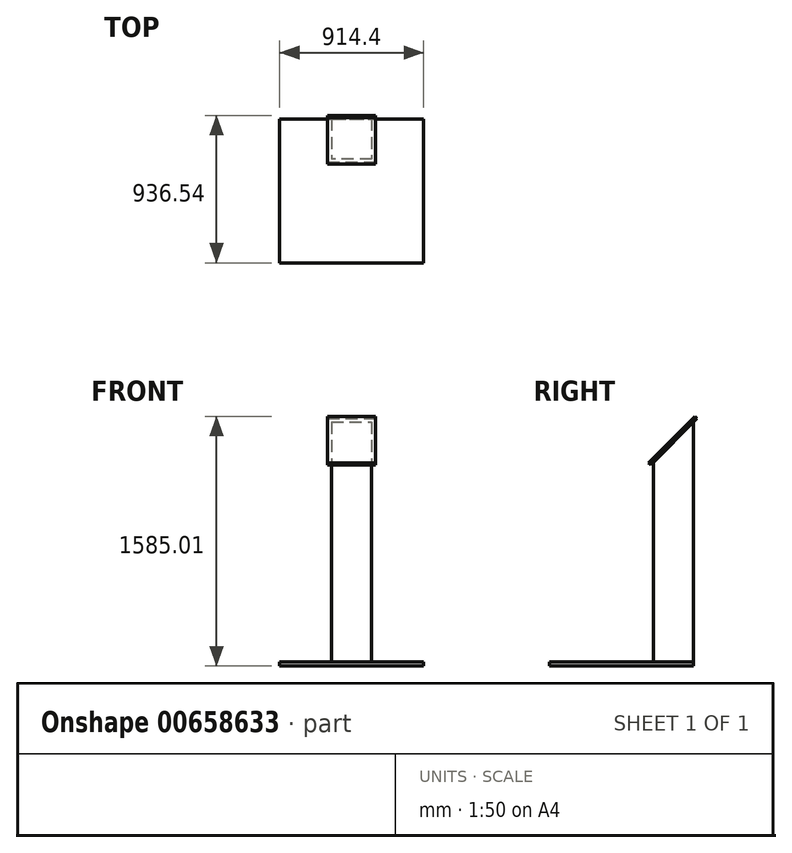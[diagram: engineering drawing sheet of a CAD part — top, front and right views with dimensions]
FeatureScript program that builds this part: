
annotation { "Feature Type Name" : "Feature", "Feature Type Description" : "" }
export const myFeature = defineFeature(function(context is Context, id is Id, definition is map)
    precondition{}
    {
        {
            var Q0;
            Q0=qCreatedBy(makeId("Top.planeOp"),FACE);
            var sketch = newSketch(context, id + "F0", { "sketchPlane" : qUnion([Q0])});
            skLineSegment(sketch, "E0.bottom", {"start": v(0, 0) * mm, "end": v(914.4, 0) * mm});
            skLineSegment(sketch, "E0.top", {"start": v(0, 914.4) * mm, "end": v(914.4, 914.4) * mm});
            skLineSegment(sketch, "E0.left", {"start": v(0, 0) * mm, "end": v(0, 914.4) * mm});
            skLineSegment(sketch, "E0.right", {"start": v(914.4, 0) * mm, "end": v(914.4, 914.4) * mm});
            skSolve(sketch);
        }
        {
            var Q0;
            Q0 = qSketchRegion(id + "F0", true);
            extrude(context, id + "F1", {"entities" : qUnion([Q0]), "depth" : 25.4 * mm, "offsetDistance" : 25.4 * mm});
        }
        {
            var Q0;
            Q0=makeQuery(id+"F1.opExtrude","CAP_FACE",FACE,{"disambiguationData":[OSD([sQuery(id+"F0.wireOp",EDGE,"E0.bottom"),sQuery(id+"F0.wireOp",EDGE,"E0.top"),sQuery(id+"F0.wireOp",EDGE,"E0.left"),sQuery(id+"F0.wireOp",EDGE,"E0.right")])],"isStart":false});
            var sketch = newSketch(context, id + "F2", { "sketchPlane" : qUnion([Q0])});
            skLineSegment(sketch, "E1.bottom", {"start": v(584.2, 914.4) * mm, "end": v(330.2, 914.4) * mm});
            skLineSegment(sketch, "E1.top", {"start": v(584.2, 660.4) * mm, "end": v(330.2, 660.4) * mm});
            skLineSegment(sketch, "E1.left", {"start": v(584.2, 914.4) * mm, "end": v(584.2, 660.4) * mm});
            skLineSegment(sketch, "E1.right", {"start": v(330.2, 914.4) * mm, "end": v(330.2, 660.4) * mm});
            skSolve(sketch);
        }
        {
            var Q0;
            Q0 = qSketchRegion(id + "F2", true);
            extrude(context, id + "F3", {"entities" : qUnion([Q0]), "operationType" : NewBodyOperationType.ADD, "depth" : 1524 * mm, "offsetDistance" : 25.4 * mm});
        }
        {
            var Q0;
            Q0=makeQuery(id+"F3.opExtrude","SWEPT_FACE",FACE,{"disambiguationData":[OSD([sQuery(id+"F2.wireOp",EDGE,"E1.left")])]});
            var sketch = newSketch(context, id + "F4", { "sketchPlane" : qUnion([Q0])});
            skLineSegment(sketch, "E2", {"start": v(914.4, 1549.4) * mm, "end": v(660.4, 1295.4) * mm});
            skSolve(sketch);
        }
        {
            var Q0;
            Q0 = qSketchRegion(id + "F4", true);
            var Q1;
            {var subQ0=sQuery(id+"F4.wireOp",EDGE,"E2");Q1=makeQuery(id+"F4.imprint","IMPRINT",FACE,{"disambiguationData":[TD([[makeQuery(id+"F4.imprint","IMPRINT",EDGE,{"derivedFrom":subQ0}),-1.0]])]});}
            extrude(context, id + "F5", {"entities" : qUnion([Q0, Q1]), "operationType" : NewBodyOperationType.REMOVE, "endBound" : BoundingType.THROUGH_ALL, "oppositeDirection" : true, "depth" : 25.4 * mm, "offsetDistance" : 25.4 * mm});
        }
        {
            var Q0;
            Q0=makeQuery(id+"F5.boolean.opBoolean","COPY",FACE,{"derivedFrom":makeQuery(id+"F5.opExtrude","SWEPT_FACE",FACE,{"disambiguationData":[OSD([sQuery(id+"F4.wireOp",EDGE,"E2")])]})});
            var sketch = newSketch(context, id + "F6", { "sketchPlane" : qUnion([Q0])});
            skLineSegment(sketch, "E3.bottom", {"start": v(304.8, 1773.48) * mm, "end": v(609.6, 1773.48) * mm});
            skLineSegment(sketch, "E3.top", {"start": v(304.8, 1357.56) * mm, "end": v(609.6, 1357.56) * mm});
            skLineSegment(sketch, "E3.left", {"start": v(304.8, 1773.48) * mm, "end": v(304.8, 1357.56) * mm});
            skLineSegment(sketch, "E3.right", {"start": v(609.6, 1773.48) * mm, "end": v(609.6, 1357.56) * mm});
            skSolve(sketch);
        }
        {
            var Q0;
            Q0 = qSketchRegion(id + "F6", true);
            extrude(context, id + "F7", {"entities" : qUnion([Q0]), "operationType" : NewBodyOperationType.ADD, "depth" : 19.05 * mm, "offsetDistance" : 25.4 * mm});
        }
    });
